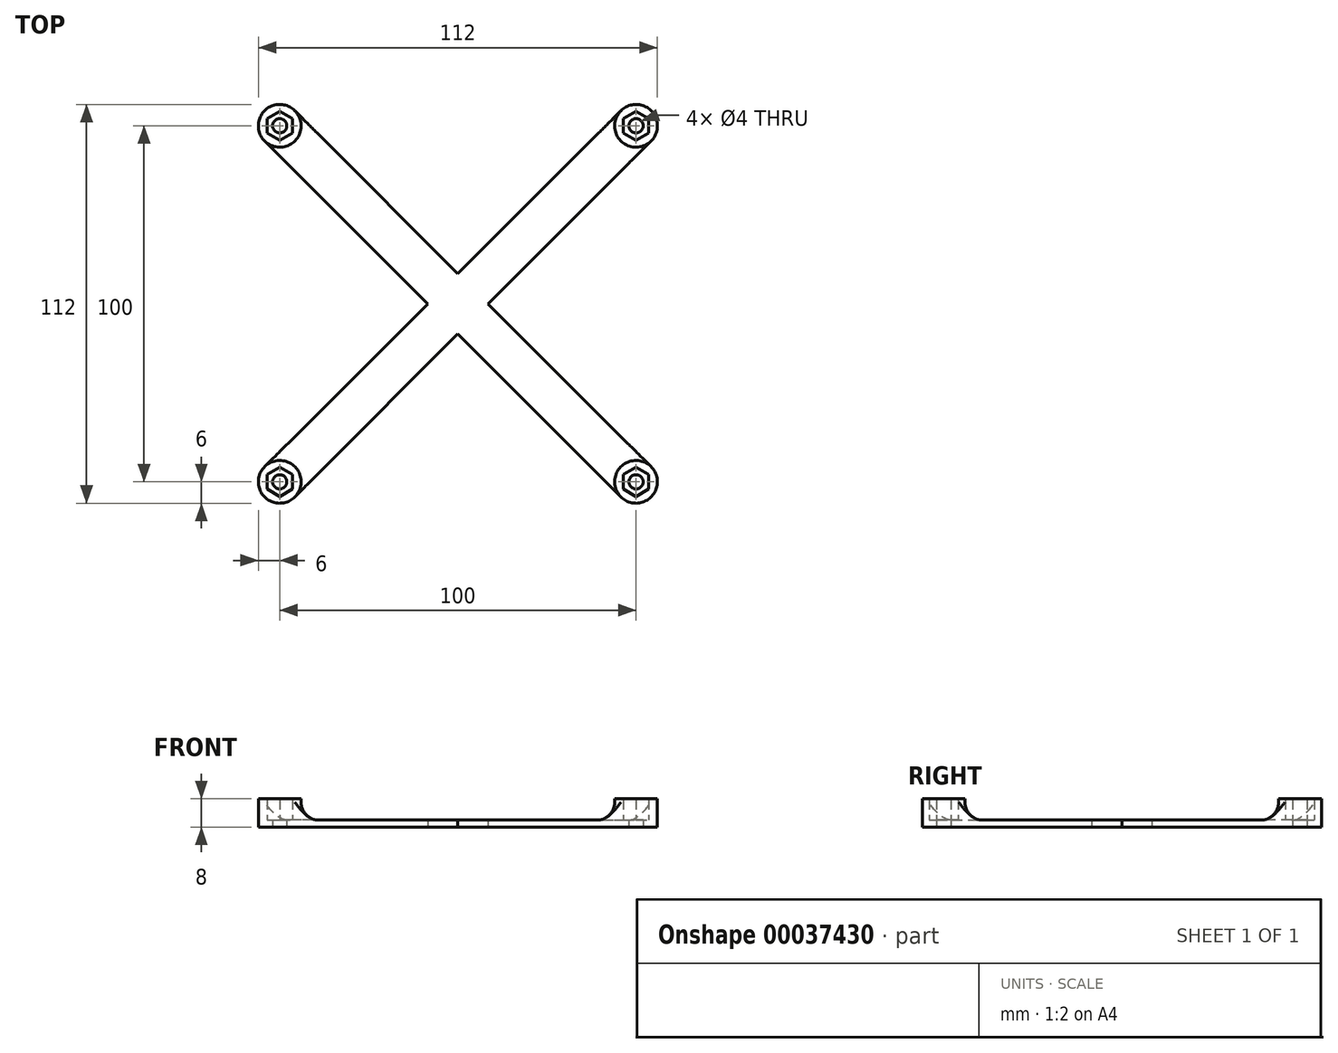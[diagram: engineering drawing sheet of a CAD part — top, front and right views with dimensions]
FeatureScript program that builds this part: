
annotation { "Feature Type Name" : "Feature", "Feature Type Description" : "" }
export const myFeature = defineFeature(function(context is Context, id is Id, definition is map)
    precondition{}
    {
        {
            var Q0;
            Q0=qCreatedBy(makeId("Top.planeOp"),FACE);
            var sketch = newSketch(context, id + "F0", { "sketchPlane" : qUnion([Q0])});
            skLineSegment(sketch, "E0", {"start": v(0, 0) * mm, "end": v(50, 0) * mm, "construction": true});
            skLineSegment(sketch, "E1", {"start": v(50, 0) * mm, "end": v(50, 50) * mm, "construction": true});
            skLineSegment(sketch, "E2", {"start": v(50, 50) * mm, "end": v(0, 50) * mm, "construction": true});
            skLineSegment(sketch, "E3", {"start": v(0, 50) * mm, "end": v(0, 0) * mm, "construction": true});
            skCircle(sketch, "E4", {"center": v(50, 50) * mm, "radius": 2 * mm});
            skCircle(sketch, "E5.cCircle", {"center": v(50, 50) * mm, "radius": 3.55 * mm, "construction": true});
            skLineSegment(sketch, "E5.0", {"start": v(46.45, 47.95) * mm, "end": v(46.45, 52.05) * mm});
            skLineSegment(sketch, "E5.1", {"start": v(46.45, 52.05) * mm, "end": v(50, 54.1) * mm});
            skLineSegment(sketch, "E5.2", {"start": v(50, 54.1) * mm, "end": v(53.55, 52.05) * mm});
            skLineSegment(sketch, "E5.3", {"start": v(53.55, 52.05) * mm, "end": v(53.55, 47.95) * mm});
            skLineSegment(sketch, "E5.4", {"start": v(53.55, 47.95) * mm, "end": v(50, 45.9) * mm});
            skLineSegment(sketch, "E5.5", {"start": v(50, 45.9) * mm, "end": v(46.45, 47.95) * mm});
            skPoint(sketch, "E5.0.midPoint", {"position": v(46.45, 50) * mm});
            skCircle(sketch, "E6", {"center": v(50, 50) * mm, "radius": 6 * mm});
            skLineSegment(sketch, "E7", {"start": v(45.76, 54.24) * mm, "end": v(0, 8.49) * mm});
            skPoint(sketch, "E7.startSnap0", {"position": v(51.77, 53.07) * mm});
            skLineSegment(sketch, "E8", {"start": v(0, 8.49) * mm, "end": v(0, 0) * mm});
            skLineSegment(sketch, "E9", {"start": v(0, 0) * mm, "end": v(8.49, 0) * mm});
            skLineSegment(sketch, "E10", {"start": v(8.49, 0) * mm, "end": v(54.24, 45.76) * mm});
            skSolve(sketch);
        }
        {
            var Q0;
            Q0=makeQuery(id+"F0.imprint","IMPRINT",FACE,{"disambiguationData":[TD([[makeQuery(id+"F0.imprint","IMPRINT",EDGE,{"derivedFrom":sQuery(id+"F0.wireOp",EDGE,"E5.0")}),1.0]])]});
            var Q1;
            Q1=makeQuery(id+"F0.imprint","IMPRINT",FACE,{"disambiguationData":[TD([[makeQuery(id+"F0.imprint","IMPRINT",EDGE,{"derivedFrom":sQuery(id+"F0.wireOp",EDGE,"E4")}),-1.0]])]});
            var Q2;
            {var subQ1=sQuery(id+"F0.wireOp",EDGE,"E7");Q2=makeQuery(id+"F0.imprint","IMPRINT",FACE,{"disambiguationData":[TD([[makeQuery(id+"F0.imprint","IMPRINT",EDGE,{"derivedFrom":subQ1}),1.0]])]});}
            extrude(context, id + "F1", {"entities" : qUnion([Q0, Q1, Q2]), "depth" : 2 * mm});
        }
        {
            var Q0;
            Q0=makeQuery(id+"F0.imprint","IMPRINT",FACE,{"disambiguationData":[TD([[makeQuery(id+"F0.imprint","IMPRINT",EDGE,{"derivedFrom":sQuery(id+"F0.wireOp",EDGE,"E5.0")}),1.0]])]});
            extrude(context, id + "F2", {"entities" : qUnion([Q0]), "operationType" : NewBodyOperationType.ADD, "depth" : 8 * mm});
        }
        {
            var Q0;
            {var subQ0=sQuery(id+"F0.wireOp",EDGE,"E6");Q0=makeQuery(id+"F2.boolean.opBoolean","INTERSECT",EDGE,{"derivedFrom":[makeQuery(id+"F1.opExtrude","CAP_FACE",FACE,{"disambiguationData":[OSD([sQuery(id+"F0.wireOp",EDGE,"E4"),subQ0,sQuery(id+"F0.wireOp",EDGE,"E7"),sQuery(id+"F0.wireOp",EDGE,"E8"),sQuery(id+"F0.wireOp",EDGE,"E9"),sQuery(id+"F0.wireOp",EDGE,"E10")])],"isStart":false}),makeQuery(id+"F2.opExtrude","SWEPT_FACE",FACE,{"disambiguationData":[OSD([subQ0])]})]});}
            fillet(context, id + "F3", {"entities" : qUnion([Q0]), "radius" : 5 * mm, "tangentPropagation" : true, "allowEdgeOverflow" : false});
        }
        {
            var Q0;
            Q0=makeQuery(id+"F1.opExtrude","SWEPT_BODY",BODY,{"disambiguationData":[OSD([sQuery(id+"F0.wireOp",EDGE,"E4"),sQuery(id+"F0.wireOp",EDGE,"E6"),sQuery(id+"F0.wireOp",EDGE,"E7"),sQuery(id+"F0.wireOp",EDGE,"E8"),sQuery(id+"F0.wireOp",EDGE,"E9"),sQuery(id+"F0.wireOp",EDGE,"E10")])]});
            var Q1;
            Q1=qCreatedBy(makeId("Front.planeOp"),FACE);
            mirror(context, id + "F4", {"operationType" : NewBodyOperationType.ADD, "entities" : qUnion([Q0]), "mirrorPlane" : qUnion([Q1])});
        }
        {
            var Q0;
            Q0=makeQuery(id+"F1.opExtrude","SWEPT_BODY",BODY,{"disambiguationData":[OSD([sQuery(id+"F0.wireOp",EDGE,"E4"),sQuery(id+"F0.wireOp",EDGE,"E6"),sQuery(id+"F0.wireOp",EDGE,"E7"),sQuery(id+"F0.wireOp",EDGE,"E8"),sQuery(id+"F0.wireOp",EDGE,"E9"),sQuery(id+"F0.wireOp",EDGE,"E10")])]});
            var Q1;
            Q1=qCreatedBy(makeId("Right.planeOp"),FACE);
            mirror(context, id + "F5", {"operationType" : NewBodyOperationType.ADD, "entities" : qUnion([Q0]), "mirrorPlane" : qUnion([Q1])});
        }
    });
